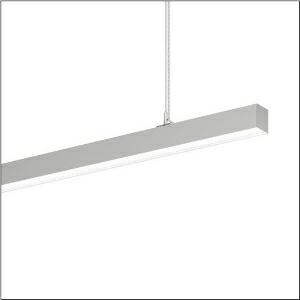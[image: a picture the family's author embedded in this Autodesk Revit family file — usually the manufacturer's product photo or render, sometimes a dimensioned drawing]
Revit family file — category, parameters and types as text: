
# Revit family: silica_21_51mx33dc4dsb
name_source: partatom
category: Lighting Fixtures
units: mm (PartAtom-declared; Revit-internal decimal feet)

## family parameters
Cut with Voids When Loaded = No
Host = Face
Light Source = No
Part Type = Normal
Room Calculation Point = No
Round Connector Dimension = Use Diameter
Shared = No

## types (1)
- --- (1 x LED, 14790 lm, 93.9 W, 4000K)
    Apparent Load = 94 VA
    CIE Flux Codes = 78 96 99 55 100
    Color Rendering = 80
    Color Temperature = 4000K
    Default Elevation = 1800 mm
    Description = Silica 21, office luminaire, primary optical cover: prismatic diffuser, of PMMA, CAT 2 (L<= 3000cd/m²), light emission: direct/indirect distribution, primary light characteristic: symmetric, installation type: suspended mounting, LED, rated luminous flux: 14.790lm, luminous efficacy: 158lm/W, light colour: 840, colour temperature: 4000K, control gear: DALI 2, with terminal, 3+2-pole, max. 2.5mm², mains connection: 220..240V, AC, 50/60Hz, rated input power: 93.9W, luminaire housing, of aluminium, metallic grey (RAL 9006), length: 3.004mm, width: 53mm, height: 53mm, protection rating (complete): IP20, insulation class (complete): insulation class I (protective earthing), certification: CE, permissible operating ambient temperature: 0..+35°C, standard: EN 50419, packaging unit: 1 piece
    Height = 53 mm
    Lamp = 1 x LED
    Lamp Light Flux = 14790 lm
    Lamp Power = 93.9 W
    Lamp count = 1
    Length = 3004 mm
    Luminous efficacy = 158 lm/W
    Manufacturer = Siteco
    ModVariant = No
    Model = 51MX33DC4DSB
    Mounting Place = Ceiling
    Mounting Type = Pendant
    Number of Poles = 1
    OnlyDefault = Yes
    Power Factor = 1
    Product Name = Silica 21
    Product group = office luminaire | ceiling pendant
    ProductGroupID = 903
    Protection Class = Protection class I
    Protection Degree = IP 20
    RLX_Detail_Level = 1
    RLX_Emergency_Light_Flux = 0 lm
    RLX_Emergency_Type = 0
    RLX_Emergency_Type_DB = No
    RlxData = <blob elided: 23429 chars, md5=b384940d>
    Socket = socket
    Standby Power = 0 W
    System Light Flux = 14790 lm
    System Power = 94 W
    Type Comments = factory setting: luminous flux: 100 % | dim-lin: 254 | 323 mA
    Type Image = l_1335864.jpg
    URL = http://relux.com
    VarID = @adj_118671
    Voltage = 0 V
    Weight = 0.00 kg
    Width = 53 mm

## geometry (parser evidence)
native form markers: Blend x4, Sweep x14
no freeform markers — native parametric forms only
